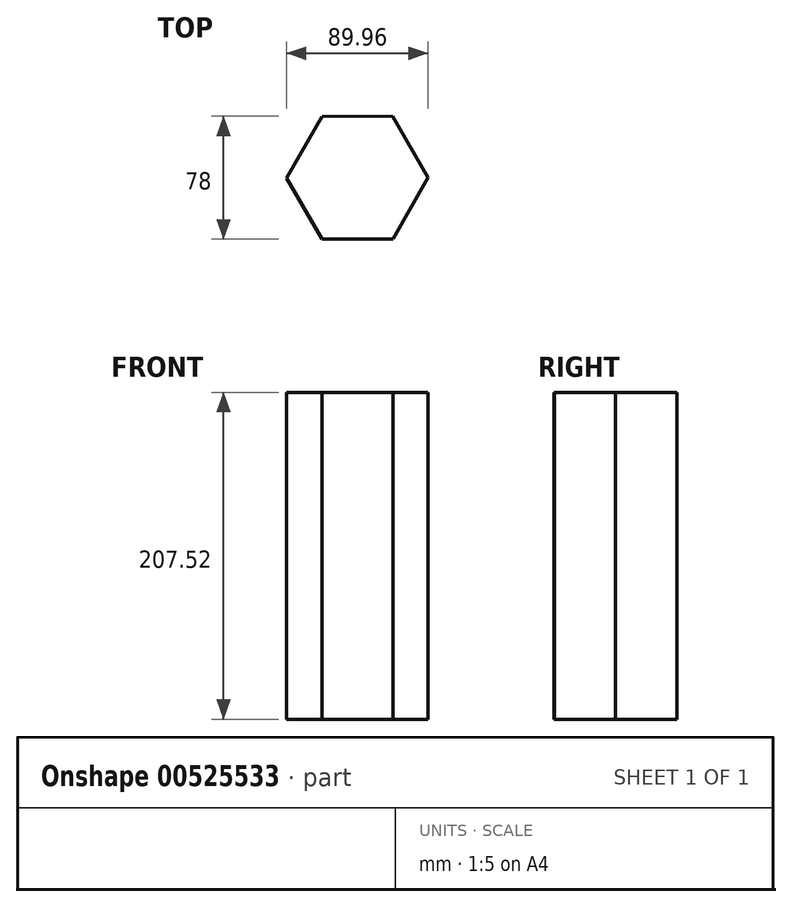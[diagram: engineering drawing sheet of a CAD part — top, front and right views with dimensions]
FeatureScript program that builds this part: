
annotation { "Feature Type Name" : "Feature", "Feature Type Description" : "" }
export const myFeature = defineFeature(function(context is Context, id is Id, definition is map)
    precondition{}
    {
        {
            var Q0;
            Q0=qCreatedBy(makeId("Top.planeOp"),FACE);
            var sketch = newSketch(context, id + "F0", { "sketchPlane" : qUnion([Q0])});
            skCircle(sketch, "E0.cCircle", {"center": v(0, 0) * mm, "radius": 38.95 * mm, "construction": true});
            skLineSegment(sketch, "E0.0", {"start": v(-22.4, -39) * mm, "end": v(-44.98, -0.1) * mm});
            skLineSegment(sketch, "E0.1", {"start": v(-44.98, -0.1) * mm, "end": v(-22.58, 38.9) * mm});
            skLineSegment(sketch, "E0.2", {"start": v(-22.58, 38.9) * mm, "end": v(22.4, 39) * mm});
            skLineSegment(sketch, "E0.3", {"start": v(22.4, 39) * mm, "end": v(44.98, 0.1) * mm});
            skLineSegment(sketch, "E0.4", {"start": v(44.98, 0.1) * mm, "end": v(22.58, -38.9) * mm});
            skLineSegment(sketch, "E0.5", {"start": v(22.58, -38.9) * mm, "end": v(-22.4, -39) * mm});
            skPoint(sketch, "E0.0.midPoint", {"position": v(-33.69, -19.55) * mm});
            skSolve(sketch);
        }
        {
            var Q0;
            Q0 = qSketchRegion(id + "F0", true);
            extrude(context, id + "F1", {"entities" : qUnion([Q0]), "depth" : 207.52 * mm, "offsetDistance" : 25.4 * mm});
        }
    });
